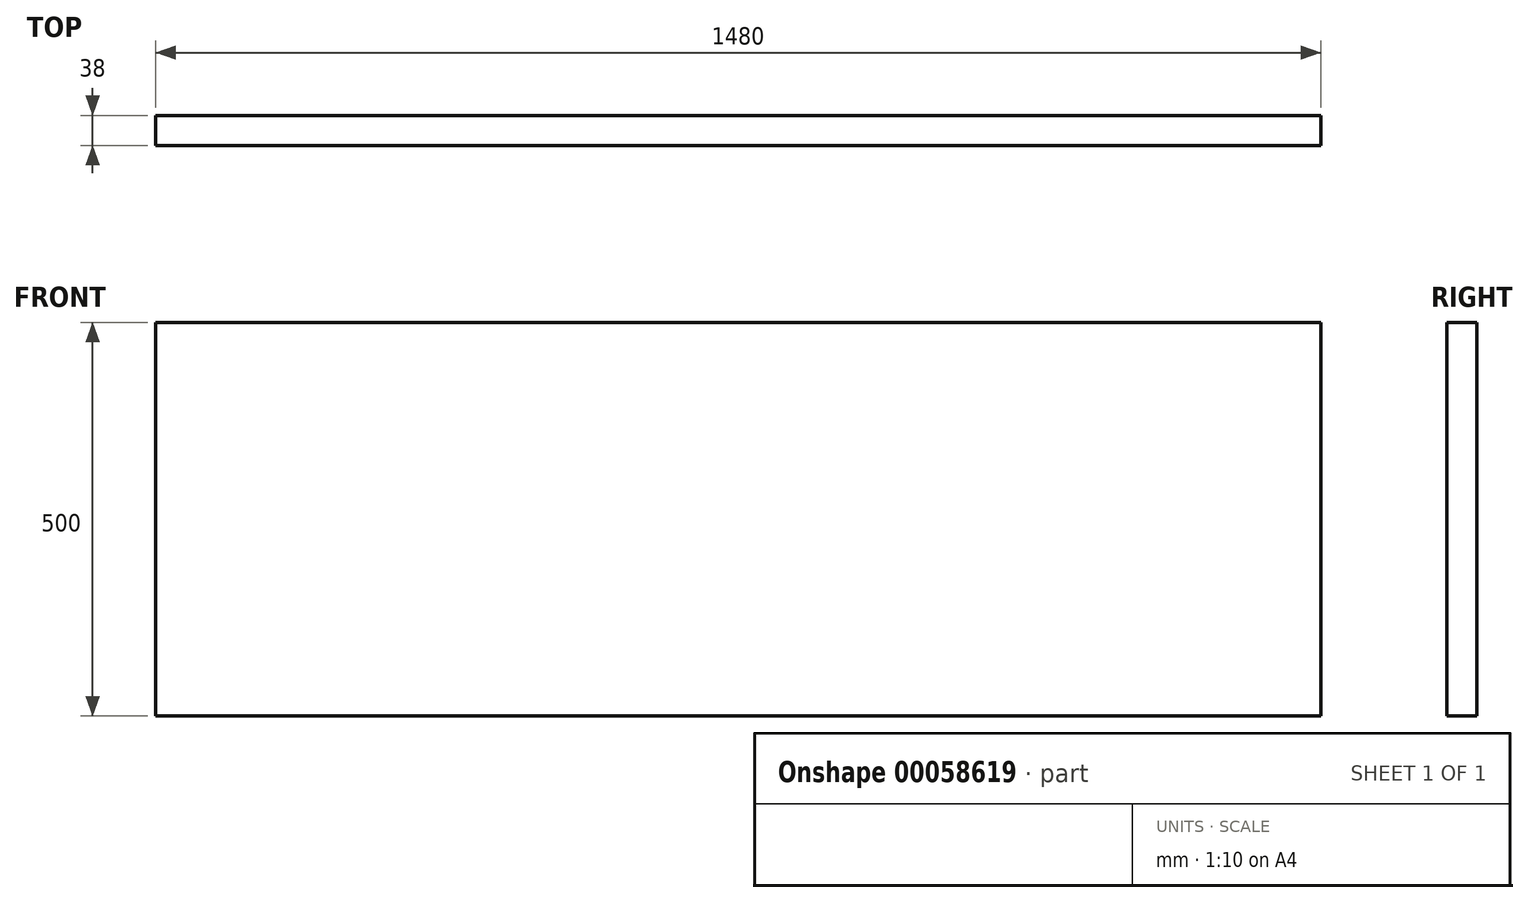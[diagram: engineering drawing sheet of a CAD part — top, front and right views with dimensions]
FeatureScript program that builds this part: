
annotation { "Feature Type Name" : "Feature", "Feature Type Description" : "" }
export const myFeature = defineFeature(function(context is Context, id is Id, definition is map)
    precondition{}
    {
        {
            var Q0;
            Q0=qCreatedBy(makeId("Front.planeOp"),FACE);
            var sketch = newSketch(context, id + "F0", { "sketchPlane" : qUnion([Q0])});
            skLineSegment(sketch, "E0", {"start": v(0, 0) * mm, "end": v(1480, 0) * mm});
            skLineSegment(sketch, "E1", {"start": v(1480, 0) * mm, "end": v(1480, 500) * mm});
            skLineSegment(sketch, "E2", {"start": v(0, 0) * mm, "end": v(0, 500) * mm});
            skLineSegment(sketch, "E3", {"start": v(0, 500) * mm, "end": v(1480, 500) * mm});
            skSolve(sketch);
        }
        {
            var Q0;
            Q0=qSketchRegion(id+"F0",true);
            extrude(context, id + "F1", {"entities" : qUnion([Q0]), "depth" : 38 * mm});
        }
    });
